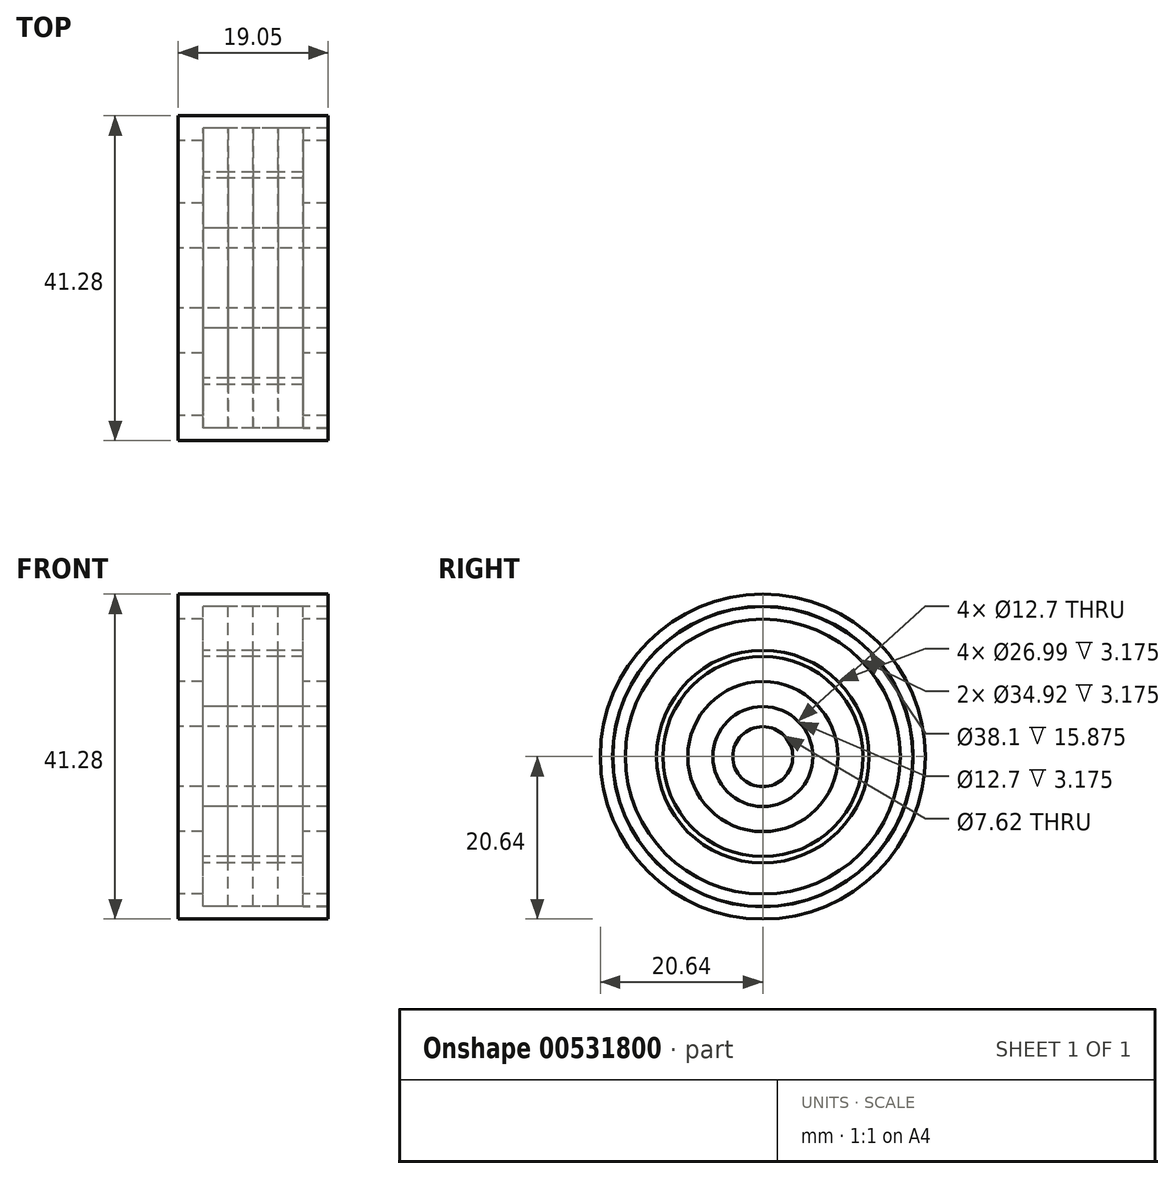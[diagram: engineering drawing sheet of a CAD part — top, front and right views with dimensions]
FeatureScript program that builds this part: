
annotation { "Feature Type Name" : "Feature", "Feature Type Description" : "" }
export const myFeature = defineFeature(function(context is Context, id is Id, definition is map)
    precondition{}
    {
        {
            var Q0;
            Q0=qCreatedBy(makeId("Right.planeOp"),FACE);
            var sketch = newSketch(context, id + "F0", { "sketchPlane" : qUnion([Q0])});
            skCircle(sketch, "E0", {"center": v(0, 0) * mm, "radius": 19.05 * mm});
            skCircle(sketch, "E1", {"center": v(0, 0) * mm, "radius": 20.64 * mm});
            skSolve(sketch);
        }
        {
            var Q0;
            Q0=makeQuery(id+"F0.imprint","IMPRINT",FACE,{"disambiguationData":[TD([[makeQuery(id+"F0.imprint","IMPRINT",EDGE,{"derivedFrom":sQuery(id+"F0.wireOp",EDGE,"E0")}),-1.0]])]});
            extrude(context, id + "F1", {"entities" : qUnion([Q0]), "depth" : 19.05 * mm, "offsetDistance" : 25.4 * mm});
        }
        {
            var Q0;
            Q0=qCreatedBy(makeId("Right.planeOp"),FACE);
            var sketch = newSketch(context, id + "F2", { "sketchPlane" : qUnion([Q0])});
            skCircle(sketch, "E2", {"center": v(0, 0) * mm, "radius": 17.46 * mm});
            skCircle(sketch, "E3", {"center": v(0, 0) * mm, "radius": 19.05 * mm});
            skSolve(sketch);
        }
        {
            var Q0;
            Q0 = qSketchRegion(id + "F2", true);
            extrude(context, id + "F3", {"entities" : qUnion([Q0]), "operationType" : NewBodyOperationType.ADD, "depth" : 3.17 * mm, "offsetDistance" : 25.4 * mm});
        }
        {
            var Q0;
            Q0=makeQuery(id+"F3.opExtrude","CAP_FACE",FACE,{"disambiguationData":[OSD([sQuery(id+"F2.wireOp",EDGE,"E2"),sQuery(id+"F2.wireOp",EDGE,"E3")])],"isStart":false});
            var sketch = newSketch(context, id + "F4", { "sketchPlane" : qUnion([Q0])});
            skCircle(sketch, "E4", {"center": v(0, 0) * mm, "radius": 19.05 * mm});
            skCircle(sketch, "E5", {"center": v(0, 0) * mm, "radius": 13.5 * mm});
            skSolve(sketch);
        }
        {
            var Q0;
            Q0 = qSketchRegion(id + "F4", true);
            extrude(context, id + "F5", {"entities" : qUnion([Q0]), "depth" : 3.17 * mm, "offsetDistance" : 25.4 * mm});
        }
        {
            var Q0;
            Q0=makeQuery(id+"F5.opExtrude","CAP_FACE",FACE,{"disambiguationData":[OSD([sQuery(id+"F4.wireOp",EDGE,"E4"),sQuery(id+"F4.wireOp",EDGE,"E5")])],"isStart":false});
            var sketch = newSketch(context, id + "F6", { "sketchPlane" : qUnion([Q0])});
            skCircle(sketch, "E6", {"center": v(0, 0) * mm, "radius": 19.05 * mm});
            skCircle(sketch, "E7", {"center": v(0, 0) * mm, "radius": 13.5 * mm});
            skSolve(sketch);
        }
        {
            var Q0;
            Q0 = qSketchRegion(id + "F6", true);
            extrude(context, id + "F7", {"entities" : qUnion([Q0]), "depth" : 3.17 * mm, "offsetDistance" : 25.4 * mm});
        }
        {
            var Q0;
            Q0=makeQuery(id+"F7.opExtrude","CAP_FACE",FACE,{"disambiguationData":[OSD([sQuery(id+"F6.wireOp",EDGE,"E6"),sQuery(id+"F6.wireOp",EDGE,"E7")])],"isStart":false});
            var sketch = newSketch(context, id + "F8", { "sketchPlane" : qUnion([Q0])});
            skCircle(sketch, "E8", {"center": v(0, 0) * mm, "radius": 19.05 * mm});
            skCircle(sketch, "E9", {"center": v(0, 0) * mm, "radius": 13.5 * mm});
            skSolve(sketch);
        }
        {
            var Q0;
            Q0 = qSketchRegion(id + "F8", true);
            extrude(context, id + "F9", {"entities" : qUnion([Q0]), "depth" : 3.17 * mm, "offsetDistance" : 25.4 * mm});
        }
        {
            var Q0;
            Q0=makeQuery(id+"F9.opExtrude","CAP_FACE",FACE,{"disambiguationData":[OSD([sQuery(id+"F8.wireOp",EDGE,"E8"),sQuery(id+"F8.wireOp",EDGE,"E9")])],"isStart":false});
            var sketch = newSketch(context, id + "F10", { "sketchPlane" : qUnion([Q0])});
            skCircle(sketch, "E10", {"center": v(0, 0) * mm, "radius": 19.05 * mm});
            skCircle(sketch, "E11", {"center": v(0, 0) * mm, "radius": 13.5 * mm});
            skSolve(sketch);
        }
        {
            var Q0;
            Q0 = qSketchRegion(id + "F10", true);
            extrude(context, id + "F11", {"entities" : qUnion([Q0]), "depth" : 3.17 * mm, "offsetDistance" : 25.4 * mm});
        }
        {
            var Q0;
            Q0=makeQuery(id+"F11.opExtrude","CAP_FACE",FACE,{"disambiguationData":[OSD([sQuery(id+"F10.wireOp",EDGE,"E10"),sQuery(id+"F10.wireOp",EDGE,"E11")])],"isStart":false});
            var sketch = newSketch(context, id + "F12", { "sketchPlane" : qUnion([Q0])});
            skCircle(sketch, "E12", {"center": v(0, 0) * mm, "radius": 17.46 * mm});
            skCircle(sketch, "E13", {"center": v(0, 0) * mm, "radius": 19.08 * mm});
            skSolve(sketch);
        }
        {
            var Q0;
            Q0 = qSketchRegion(id + "F12", true);
            extrude(context, id + "F13", {"entities" : qUnion([Q0]), "depth" : 3.17 * mm, "offsetDistance" : 25.4 * mm});
        }
        {
            var Q0;
            Q0=qCreatedBy(makeId("Right.planeOp"),FACE);
            var sketch = newSketch(context, id + "F14", { "sketchPlane" : qUnion([Q0])});
            skCircle(sketch, "E14", {"center": v(0, 0) * mm, "radius": 9.53 * mm});
            skCircle(sketch, "E15", {"center": v(0, 0) * mm, "radius": 6.35 * mm});
            skCircle(sketch, "E16", {"center": v(0, 0) * mm, "radius": 3.81 * mm});
            skSolve(sketch);
        }
        {
            var Q0;
            Q0 = qSketchRegion(id + "F14", true);
            extrude(context, id + "F15", {"entities" : qUnion([Q0]), "depth" : 3.17 * mm, "offsetDistance" : 25.4 * mm});
        }
        {
            var Q0;
            Q0=makeQuery(id+"F14.imprint","IMPRINT",FACE,{"disambiguationData":[TD([[makeQuery(id+"F14.imprint","IMPRINT",EDGE,{"derivedFrom":sQuery(id+"F14.wireOp",EDGE,"E15")}),1.0]])]});
            var Q1;
            Q1=makeQuery(id+"F1.opExtrude","CAP_FACE",FACE,{"disambiguationData":[OSD([sQuery(id+"F0.wireOp",EDGE,"E0"),sQuery(id+"F0.wireOp",EDGE,"E1")])],"isStart":false});
            extrude(context, id + "F16", {"entities" : qUnion([Q0]), "operationType" : NewBodyOperationType.ADD, "endBound" : BoundingType.UP_TO_SURFACE, "depth" : 25.4 * mm, "endBoundEntityFace" : qUnion([Q1]), "offsetDistance" : 25.4 * mm});
        }
        {
            var Q0;
            Q0=makeQuery(id+"F15.opExtrude","CAP_FACE",FACE,{"disambiguationData":[OSD([sQuery(id+"F14.wireOp",EDGE,"E14"),sQuery(id+"F14.wireOp",EDGE,"E15")])],"isStart":false});
            var sketch = newSketch(context, id + "F17", { "sketchPlane" : qUnion([Q0])});
            skCircle(sketch, "E17", {"center": v(0, 0) * mm, "radius": 12.7 * mm});
            skCircle(sketch, "E18", {"center": v(0, 0) * mm, "radius": 6.35 * mm});
            skSolve(sketch);
        }
        {
            var Q0;
            Q0 = qSketchRegion(id + "F17", true);
            extrude(context, id + "F18", {"entities" : qUnion([Q0]), "depth" : 3.17 * mm, "offsetDistance" : 25.4 * mm});
        }
        {
            var Q0;
            Q0=makeQuery(id+"F18.opExtrude","CAP_FACE",FACE,{"disambiguationData":[OSD([sQuery(id+"F17.wireOp",EDGE,"E17"),sQuery(id+"F17.wireOp",EDGE,"E18")])],"isStart":false});
            var sketch = newSketch(context, id + "F19", { "sketchPlane" : qUnion([Q0])});
            skCircle(sketch, "E19", {"center": v(0, 0) * mm, "radius": 12.7 * mm});
            skCircle(sketch, "E20", {"center": v(0, 0) * mm, "radius": 6.35 * mm});
            skSolve(sketch);
        }
        {
            var Q0;
            Q0 = qSketchRegion(id + "F19", true);
            extrude(context, id + "F20", {"entities" : qUnion([Q0]), "depth" : 3.17 * mm, "offsetDistance" : 25.4 * mm});
        }
        {
            var Q0;
            Q0=makeQuery(id+"F20.opExtrude","CAP_FACE",FACE,{"disambiguationData":[OSD([sQuery(id+"F19.wireOp",EDGE,"E19"),sQuery(id+"F19.wireOp",EDGE,"E20")])],"isStart":false});
            var sketch = newSketch(context, id + "F21", { "sketchPlane" : qUnion([Q0])});
            skCircle(sketch, "E21", {"center": v(0, 0) * mm, "radius": 12.7 * mm});
            skCircle(sketch, "E22", {"center": v(0, 0) * mm, "radius": 6.35 * mm});
            skSolve(sketch);
        }
        {
            var Q0;
            Q0 = qSketchRegion(id + "F21", true);
            extrude(context, id + "F22", {"entities" : qUnion([Q0]), "depth" : 3.17 * mm, "offsetDistance" : 25.4 * mm});
        }
        {
            var Q0;
            Q0=makeQuery(id+"F22.opExtrude","CAP_FACE",FACE,{"disambiguationData":[OSD([sQuery(id+"F21.wireOp",EDGE,"E21"),sQuery(id+"F21.wireOp",EDGE,"E22")])],"isStart":false});
            var sketch = newSketch(context, id + "F23", { "sketchPlane" : qUnion([Q0])});
            skCircle(sketch, "E23", {"center": v(0, 0) * mm, "radius": 12.7 * mm});
            skCircle(sketch, "E24", {"center": v(0, 0) * mm, "radius": 6.35 * mm});
            skSolve(sketch);
        }
        {
            var Q0;
            Q0 = qSketchRegion(id + "F23", true);
            extrude(context, id + "F24", {"entities" : qUnion([Q0]), "depth" : 3.17 * mm, "offsetDistance" : 25.4 * mm});
        }
        {
            var Q0;
            Q0=makeQuery(id+"F24.opExtrude","CAP_FACE",FACE,{"disambiguationData":[OSD([sQuery(id+"F23.wireOp",EDGE,"E23"),sQuery(id+"F23.wireOp",EDGE,"E24")])],"isStart":false});
            var sketch = newSketch(context, id + "F25", { "sketchPlane" : qUnion([Q0])});
            skCircle(sketch, "E25", {"center": v(0, 0) * mm, "radius": 9.53 * mm});
            skCircle(sketch, "E26", {"center": v(0, 0) * mm, "radius": 6.35 * mm});
            skSolve(sketch);
        }
        {
            var Q0;
            Q0 = qSketchRegion(id + "F25", true);
            extrude(context, id + "F26", {"entities" : qUnion([Q0]), "depth" : 3.17 * mm, "offsetDistance" : 25.4 * mm});
        }
    });
